# Revit family: 室内组合消火栓箱 - 双栓 - 背面单进水接口带卷盘
name_source: partatom
category: 机械设备
revit_build: Autodesk Revit 2016 (Build: 20150110_1515(x64)
units: mm (PartAtom-declared; Revit-internal decimal feet)

## family parameters
主体 = 面
共享 = 否
加载时剪切的空心 = 是
圆形连接件大小 = 使用半径
房间计算点 = 否
零件类型 = 标准

## types (3) — shared parameters
B = 750  [stored 2.46063 ft]
G = 140  [stored 0.459318 ft]
偏移 = 94
公称半径 = 33 mm
公称直径 = 65 mm
半径 = 197
箱材质 = <按类别>
默认高程 = 1100

## per-type parameters (varying)
| type | A | C | D | F | H |
| 类型 D - 背面 - 65 mm | 1900  [stored 6.2336 ft] | 240  [stored 0.787402 ft] | 620  [stored 2.03412 ft] | 220  [stored 0.721785 ft] | 720  [stored 2.3622 ft] |
| 薄型 1 - 背面 - 65 mm | 2000  [stored 6.56168 ft] | 160  [stored 0.524934 ft] | 780  [stored 2.55906 ft] | 250  [stored 0.82021 ft] | 680  [stored 2.23097 ft] |
| 薄型 2 - 背面 - 65 mm | 2000  [stored 6.56168 ft] | 180  [stored 0.590551 ft] | 780  [stored 2.55906 ft] | 250  [stored 0.82021 ft] | 680  [stored 2.23097 ft] |

note: [stored X ft] marks values corroborated as IEEE doubles in the binary element streams (Revit-internal decimal feet)
